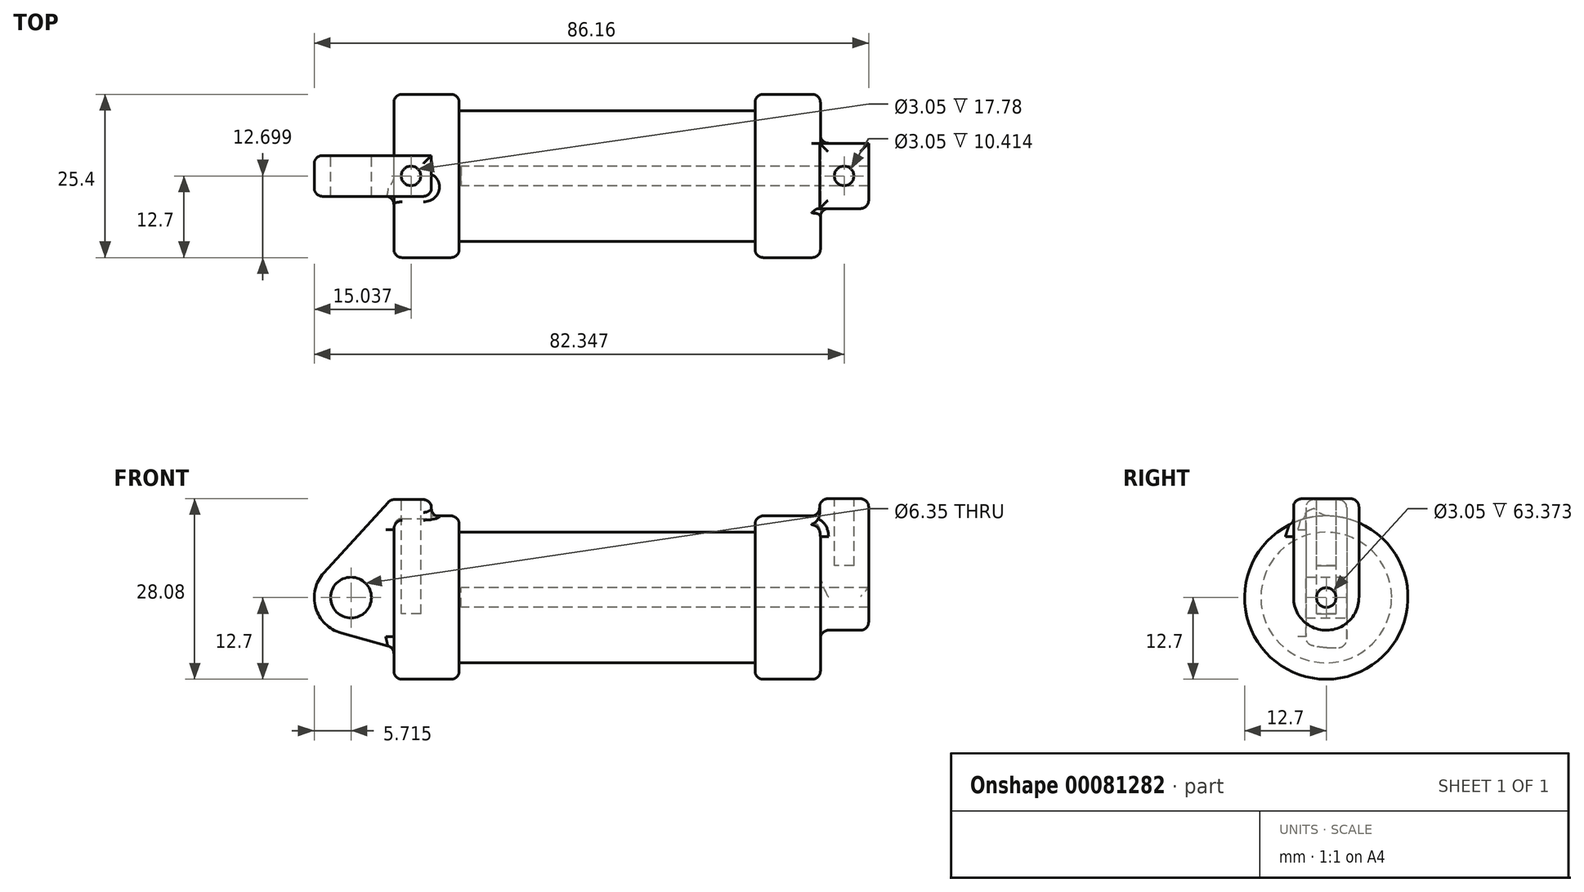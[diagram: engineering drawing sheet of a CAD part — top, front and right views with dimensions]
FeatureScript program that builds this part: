
annotation { "Feature Type Name" : "Feature", "Feature Type Description" : "" }
export const myFeature = defineFeature(function(context is Context, id is Id, definition is map)
    precondition{}
    {
        {
            var Q0;
            Q0=qCreatedBy(makeId("Front.planeOp"),FACE);
            var sketch = newSketch(context, id + "F0", { "sketchPlane" : qUnion([Q0])});
            skLineSegment(sketch, "E0", {"start": v(0, 0) * mm, "end": v(0, 12.7) * mm});
            skLineSegment(sketch, "E1", {"start": v(0, 12.7) * mm, "end": v(10.16, 12.7) * mm});
            skLineSegment(sketch, "E2", {"start": v(10.16, 12.7) * mm, "end": v(10.16, 10.16) * mm});
            skLineSegment(sketch, "E3", {"start": v(10.16, 10.16) * mm, "end": v(56.13, 10.16) * mm});
            skLineSegment(sketch, "E4", {"start": v(56.13, 10.16) * mm, "end": v(56.13, 12.7) * mm});
            skLineSegment(sketch, "E5", {"start": v(56.13, 12.7) * mm, "end": v(66.3, 12.7) * mm});
            skLineSegment(sketch, "E6", {"start": v(66.3, 12.7) * mm, "end": v(66.3, 0) * mm});
            skLineSegment(sketch, "E7", {"start": v(66.3, 0) * mm, "end": v(0, 0) * mm});
            skLineSegment(sketch, "E8", {"start": v(5.84, 15.24) * mm, "end": v(-0.5, 15.24) * mm});
            skLineSegment(sketch, "E9", {"start": v(-0.5, 15.24) * mm, "end": v(-10.88, 3.85) * mm});
            skLineSegment(sketch, "E10", {"start": v(0, 0) * mm, "end": v(-6.65, 0) * mm});
            skCircle(sketch, "E11", {"center": v(-6.65, 0) * mm, "radius": 5.72 * mm});
            skCircle(sketch, "E12", {"center": v(-6.65, 0) * mm, "radius": 3.18 * mm});
            skLineSegment(sketch, "E13", {"start": v(5.84, 15.24) * mm, "end": v(5.84, -9.4) * mm});
            skLineSegment(sketch, "E14", {"start": v(5.84, -9.4) * mm, "end": v(-8.18, -5.5) * mm});
            skSolve(sketch);
        }
        {
            var Q0;
            {var subQ0=sQuery(id+"F0.wireOp",EDGE,"E2");Q0=makeQuery(id+"F0.imprint","IMPRINT",FACE,{"disambiguationData":[TD([[makeQuery(id+"F0.imprint","IMPRINT",EDGE,{"derivedFrom":subQ0}),-1.0]])]});}
            var Q1;
            {var subQ0=sQuery(id+"F0.wireOp",EDGE,"E0");Q1=makeQuery(id+"F0.imprint","IMPRINT",FACE,{"disambiguationData":[TD([[makeQuery(id+"F0.imprint","IMPRINT",EDGE,{"derivedFrom":subQ0}),-1.0]])]});}
            var Q2;
            Q2=sQuery(id+"F0.wireOp",EDGE,"E7");
            revolve(context, id + "F1", {"entities" : qUnion([Q0, Q1]), "axis" : qUnion([Q2]), "revolveType" : RevolveType.FULL});
        }
        {
            var Q0;
            {var subQ3=sQuery(id+"F0.wireOp",EDGE,"E0");Q0=makeQuery(id+"F0.imprint","IMPRINT",FACE,{"disambiguationData":[TD([[makeQuery(id+"F0.imprint","IMPRINT",EDGE,{"derivedFrom":subQ3}),1.0]])]});}
            var Q1;
            {var subQ0=sQuery(id+"F0.wireOp",EDGE,"E0");Q1=makeQuery(id+"F0.imprint","IMPRINT",FACE,{"disambiguationData":[TD([[makeQuery(id+"F0.imprint","IMPRINT",EDGE,{"derivedFrom":subQ0}),-1.0]])]});}
            var Q2;
            {var subQ4=sQuery(id+"F0.wireOp",EDGE,"E12");Q2=makeQuery(id+"F0.imprint","IMPRINT",FACE,{"disambiguationData":[TD([[makeQuery(id+"F0.imprint","IMPRINT",EDGE,{"derivedFrom":subQ4}),-1.0]])]});}
            var Q3;
            {var subQ0=sQuery(id+"F0.wireOp",EDGE,"E14");Q3=makeQuery(id+"F0.imprint","IMPRINT",FACE,{"disambiguationData":[TD([[makeQuery(id+"F0.imprint","IMPRINT",EDGE,{"derivedFrom":subQ0}),-1.0]])]});}
            extrude(context, id + "F2", {"entities" : qUnion([Q0, Q1, Q2, Q3]), "operationType" : NewBodyOperationType.ADD, "endBound" : BoundingType.SYMMETRIC, "depth" : 6.35 * mm});
        }
        {
            var Q0;
            Q0=makeQuery(id+"F1.opRevolve","SWEPT_FACE",FACE,{"disambiguationData":[OSD([sQuery(id+"F0.wireOp",EDGE,"E6")])]});
            var sketch = newSketch(context, id + "F3", { "sketchPlane" : qUnion([Q0])});
            skCircle(sketch, "E15", {"center": v(0, 0) * mm, "radius": 5.08 * mm});
            skCircle(sketch, "E16", {"center": v(0, 0) * mm, "radius": 1.52 * mm});
            skLineSegment(sketch, "E17", {"start": v(-5.08, 0) * mm, "end": v(-5.08, 15.38) * mm});
            skLineSegment(sketch, "E18", {"start": v(-5.08, 15.38) * mm, "end": v(5.08, 15.38) * mm});
            skLineSegment(sketch, "E19", {"start": v(5.08, 0.14) * mm, "end": v(5.08, 15.38) * mm});
            skSolve(sketch);
        }
        {
            var Q0;
            Q0 = qSketchRegion(id + "F3", true);
            extrude(context, id + "F4", {"entities" : qUnion([Q0]), "operationType" : NewBodyOperationType.ADD, "depth" : 7.5 * mm, "hasSecondDirection" : true, "secondDirectionOppositeDirection" : true, "secondDirectionDepth" : 0.13 * mm});
        }
        {
            var Q0;
            Q0=makeQuery(id+"F3.imprint","IMPRINT",FACE,{"disambiguationData":[TD([[makeQuery(id+"F3.imprint","IMPRINT",EDGE,{"derivedFrom":sQuery(id+"F3.wireOp",EDGE,"E16")}),1.0]])]});
            extrude(context, id + "F5", {"entities" : qUnion([Q0]), "operationType" : NewBodyOperationType.REMOVE, "oppositeDirection" : true, "depth" : 55.88 * mm});
        }
        {
            var Q0;
            Q0=makeQuery(id+"F2.opExtrude","SWEPT_FACE",FACE,{"disambiguationData":[OSD([sQuery(id+"F0.wireOp",EDGE,"E8")])]});
            var sketch = newSketch(context, id + "F6", { "sketchPlane" : qUnion([Q0])});
            skCircle(sketch, "E20", {"center": v(2.67, 0) * mm, "radius": 1.52 * mm});
            skSolve(sketch);
        }
        {
            var Q0;
            Q0 = qSketchRegion(id + "F6", true);
            extrude(context, id + "F7", {"entities" : qUnion([Q0]), "operationType" : NewBodyOperationType.REMOVE, "oppositeDirection" : true, "depth" : 17.78 * mm});
        }
        {
            var Q0;
            Q0=makeQuery(id+"F4.opExtrude","SWEPT_FACE",FACE,{"disambiguationData":[OSD([sQuery(id+"F3.wireOp",EDGE,"E18")])]});
            var sketch = newSketch(context, id + "F8", { "sketchPlane" : qUnion([Q0])});
            skCircle(sketch, "E21", {"center": v(69.98, 0) * mm, "radius": 1.52 * mm});
            skSolve(sketch);
        }
        {
            var Q0;
            Q0=makeQuery(id+"F8.imprint","IMPRINT",FACE,{"disambiguationData":[TD([[makeQuery(id+"F8.imprint","IMPRINT",EDGE,{"derivedFrom":sQuery(id+"F8.wireOp",EDGE,"E21")}),1.0]])]});
            extrude(context, id + "F9", {"entities" : qUnion([Q0]), "operationType" : NewBodyOperationType.REMOVE, "oppositeDirection" : true, "depth" : 10.4 * mm});
        }
        {
            var Q0;
            Q0=makeQuery(id+"F1.opRevolve","SWEPT_EDGE",EDGE,{"disambiguationData":[OSD([sQuery(id+"F0.wireOp",EDGE,"E1"),sQuery(id+"F0.wireOp",EDGE,"E2")])]});
            var Q1;
            Q1=makeQuery(id+"F1.opRevolve","SWEPT_EDGE",EDGE,{"disambiguationData":[OSD([sQuery(id+"F0.wireOp",EDGE,"E0"),sQuery(id+"F0.wireOp",EDGE,"E1")])]});
            var Q2;
            Q2=makeQuery(id+"F1.opRevolve","SWEPT_EDGE",EDGE,{"disambiguationData":[OSD([sQuery(id+"F0.wireOp",EDGE,"E4"),sQuery(id+"F0.wireOp",EDGE,"E5")])]});
            var Q3;
            Q3=makeQuery(id+"F1.opRevolve","SWEPT_EDGE",EDGE,{"disambiguationData":[OSD([sQuery(id+"F0.wireOp",EDGE,"E5"),sQuery(id+"F0.wireOp",EDGE,"E6")])]});
            fillet(context, id + "F10", {"entities" : qUnion([Q0, Q1, Q2, Q3]), "radius" : 1.27 * mm, "tangentPropagation" : true, "allowEdgeOverflow" : false});
        }
        {
            var Q0;
            Q0=makeQuery(id+"F4.opExtrude","CAP_EDGE",EDGE,{"disambiguationData":[OSD([sQuery(id+"F3.wireOp",EDGE,"E15")])],"isStart":false});
            var Q1;
            Q1=makeQuery(id+"F4.boolean.opBoolean","INTERSECT",EDGE,{"derivedFrom":[makeQuery(id+"F1.opRevolve","SWEPT_FACE",FACE,{"disambiguationData":[OSD([sQuery(id+"F0.wireOp",EDGE,"E6")])]}),makeQuery(id+"F4.opExtrude","SWEPT_FACE",FACE,{"disambiguationData":[OSD([sQuery(id+"F3.wireOp",EDGE,"E15")])]})]});
            var Q2;
            Q2=makeQuery(id+"F4.opExtrude","SWEPT_EDGE",EDGE,{"disambiguationData":[OSD([sQuery(id+"F3.wireOp",EDGE,"E15"),sQuery(id+"F3.wireOp",EDGE,"E17")])]});
            var Q3;
            Q3=makeQuery(id+"F4.opExtrude","SWEPT_EDGE",EDGE,{"disambiguationData":[OSD([sQuery(id+"F3.wireOp",EDGE,"E15"),sQuery(id+"F3.wireOp",EDGE,"E19")])]});
            var Q4;
            Q4=makeQuery(id+"F4.opExtrude","CAP_EDGE",EDGE,{"disambiguationData":[OSD([sQuery(id+"F3.wireOp",EDGE,"E18")])],"isStart":false});
            var Q5;
            Q5=makeQuery(id+"F4.opExtrude","CAP_EDGE",EDGE,{"disambiguationData":[OSD([sQuery(id+"F3.wireOp",EDGE,"E18")])],"isStart":true});
            var Q6;
            Q6=makeQuery(id+"F4.opExtrude","SWEPT_EDGE",EDGE,{"disambiguationData":[OSD([sQuery(id+"F3.wireOp",EDGE,"E18"),sQuery(id+"F3.wireOp",EDGE,"E19")])]});
            var Q7;
            Q7=makeQuery(id+"F4.opExtrude","SWEPT_EDGE",EDGE,{"disambiguationData":[OSD([sQuery(id+"F3.wireOp",EDGE,"E17"),sQuery(id+"F3.wireOp",EDGE,"E18")])]});
            fillet(context, id + "F11", {"entities" : qUnion([Q0, Q1, Q2, Q3, Q4, Q5, Q6, Q7]), "radius" : 1.27 * mm, "tangentPropagation" : true, "allowEdgeOverflow" : false});
        }
        {
            var Q0;
            Q0=makeQuery(id+"F4.boolean.opBoolean","INTERSECT",EDGE,{"derivedFrom":[makeQuery(id+"F1.opRevolve","SWEPT_FACE",FACE,{"disambiguationData":[OSD([sQuery(id+"F0.wireOp",EDGE,"E5")])]}),makeQuery(id+"F4.opExtrude","CAP_FACE",FACE,{"disambiguationData":[OSD([sQuery(id+"F3.wireOp",EDGE,"E15"),sQuery(id+"F3.wireOp",EDGE,"E16"),sQuery(id+"F3.wireOp",EDGE,"E17"),sQuery(id+"F3.wireOp",EDGE,"E18"),sQuery(id+"F3.wireOp",EDGE,"E19")])],"isStart":true})]});
            fillet(context, id + "F12", {"entities" : qUnion([Q0]), "radius" : 1.27 * mm, "tangentPropagation" : true, "allowEdgeOverflow" : false});
        }
        {
            var Q0;
            Q0=makeQuery(id+"F2.opExtrude","CAP_EDGE",EDGE,{"disambiguationData":[OSD([sQuery(id+"F0.wireOp",EDGE,"E9")])],"isStart":false});
            var Q1;
            Q1=makeQuery(id+"F2.opExtrude","CAP_EDGE",EDGE,{"disambiguationData":[OSD([sQuery(id+"F0.wireOp",EDGE,"E9")])],"isStart":true});
            var Q2;
            Q2=makeQuery(id+"F2.opExtrude","CAP_EDGE",EDGE,{"disambiguationData":[OSD([sQuery(id+"F0.wireOp",EDGE,"E8")])],"isStart":false});
            var Q3;
            Q3=makeQuery(id+"F2.opExtrude","SWEPT_EDGE",EDGE,{"disambiguationData":[OSD([sQuery(id+"F0.wireOp",EDGE,"E8"),sQuery(id+"F0.wireOp",EDGE,"E9")])]});
            var Q4;
            Q4=makeQuery(id+"F2.opExtrude","CAP_EDGE",EDGE,{"disambiguationData":[OSD([sQuery(id+"F0.wireOp",EDGE,"E8")])],"isStart":true});
            var Q5;
            Q5=makeQuery(id+"F2.opExtrude","SWEPT_EDGE",EDGE,{"disambiguationData":[OSD([sQuery(id+"F0.wireOp",EDGE,"E8"),sQuery(id+"F0.wireOp",EDGE,"E13")])]});
            var Q6;
            Q6=makeQuery(id+"F2.opExtrude","CAP_EDGE",EDGE,{"disambiguationData":[OSD([sQuery(id+"F0.wireOp",EDGE,"E13")])],"isStart":false});
            var Q7;
            Q7=makeQuery(id+"F2.boolean.opBoolean","INTERSECT",EDGE,{"derivedFrom":[makeQuery(id+"F1.opRevolve","SWEPT_FACE",FACE,{"disambiguationData":[OSD([sQuery(id+"F0.wireOp",EDGE,"E1")])]}),makeQuery(id+"F2.opExtrude","CAP_FACE",FACE,{"disambiguationData":[OSD([sQuery(id+"F0.wireOp",EDGE,"E8"),sQuery(id+"F0.wireOp",EDGE,"E9"),sQuery(id+"F0.wireOp",EDGE,"E11"),sQuery(id+"F0.wireOp",EDGE,"E12"),sQuery(id+"F0.wireOp",EDGE,"E13"),sQuery(id+"F0.wireOp",EDGE,"E14")])],"isStart":false})]});
            var Q8;
            Q8=makeQuery(id+"F10.opFillet","BLEND_EDGE",EDGE,{"blendedFrom":[makeQuery(id+"F1.opRevolve","SWEPT_EDGE",EDGE,{"disambiguationData":[OSD([sQuery(id+"F0.wireOp",EDGE,"E0"),sQuery(id+"F0.wireOp",EDGE,"E1")])]}),makeQuery(id+"F2.opExtrude","CAP_FACE",FACE,{"disambiguationData":[OSD([sQuery(id+"F0.wireOp",EDGE,"E8"),sQuery(id+"F0.wireOp",EDGE,"E9"),sQuery(id+"F0.wireOp",EDGE,"E11"),sQuery(id+"F0.wireOp",EDGE,"E12"),sQuery(id+"F0.wireOp",EDGE,"E13"),sQuery(id+"F0.wireOp",EDGE,"E14")])],"isStart":false})],"blendedInto":[makeQuery(id+"F2.opExtrude","CAP_FACE",FACE,{"disambiguationData":[OSD([sQuery(id+"F0.wireOp",EDGE,"E8"),sQuery(id+"F0.wireOp",EDGE,"E9"),sQuery(id+"F0.wireOp",EDGE,"E11"),sQuery(id+"F0.wireOp",EDGE,"E12"),sQuery(id+"F0.wireOp",EDGE,"E13"),sQuery(id+"F0.wireOp",EDGE,"E14")])],"isStart":false})]});
            var Q9;
            Q9=makeQuery(id+"F2.opExtrude","CAP_EDGE",EDGE,{"disambiguationData":[OSD([sQuery(id+"F0.wireOp",EDGE,"E11")])],"isStart":false});
            fillet(context, id + "F13", {"entities" : qUnion([Q0, Q1, Q2, Q3, Q4, Q5, Q6, Q7, Q8, Q9]), "radius" : 1.27 * mm, "tangentPropagation" : true, "allowEdgeOverflow" : false});
        }
    });
